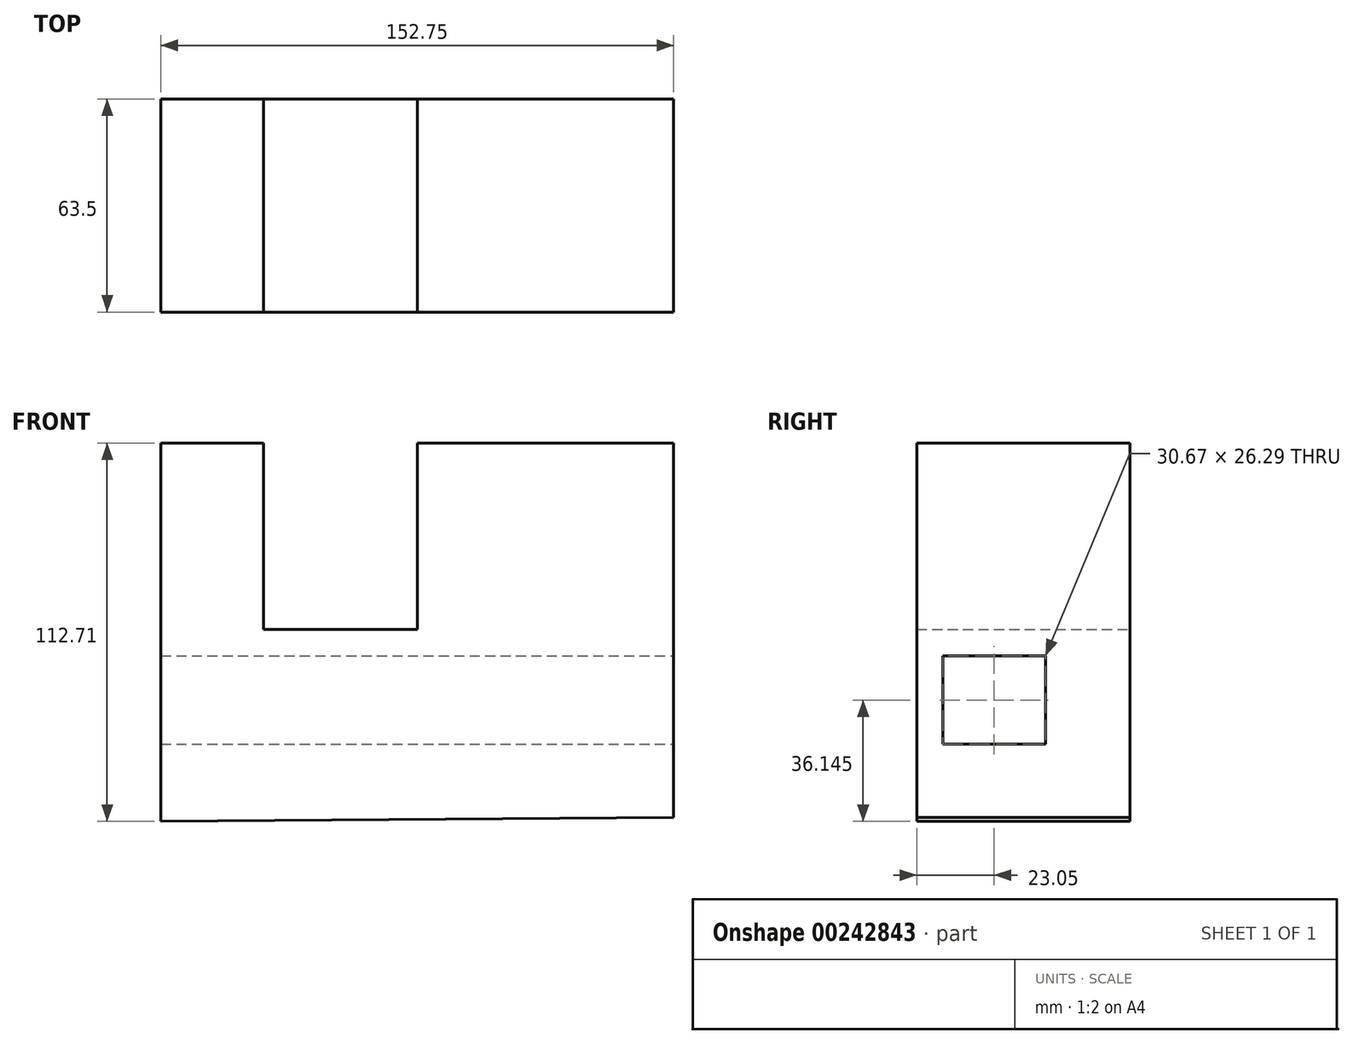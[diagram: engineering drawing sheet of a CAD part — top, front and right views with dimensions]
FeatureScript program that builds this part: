
annotation { "Feature Type Name" : "Feature", "Feature Type Description" : "" }
export const myFeature = defineFeature(function(context is Context, id is Id, definition is map)
    precondition{}
    {
        {
            var Q0;
            Q0=qCreatedBy(makeId("Front.planeOp"),FACE);
            var sketch = newSketch(context, id + "F0", { "sketchPlane" : qUnion([Q0])});
            skLineSegment(sketch, "E0", {"start": v(-76.39, 55.52) * mm, "end": v(-76.39, -57.19) * mm});
            skLineSegment(sketch, "E1", {"start": v(-76.39, 55.52) * mm, "end": v(-45.83, 55.52) * mm});
            skLineSegment(sketch, "E2", {"start": v(-45.83, 55.68) * mm, "end": v(-45.83, 0) * mm});
            skLineSegment(sketch, "E3", {"start": v(-45.83, 0) * mm, "end": v(0, 0) * mm});
            skLineSegment(sketch, "E4", {"start": v(0, 0) * mm, "end": v(0, 55.52) * mm});
            skLineSegment(sketch, "E5", {"start": v(0, 55.52) * mm, "end": v(76.36, 55.52) * mm});
            skLineSegment(sketch, "E6", {"start": v(76.36, 55.52) * mm, "end": v(76.36, -56.02) * mm});
            skLineSegment(sketch, "E7", {"start": v(76.36, -56.02) * mm, "end": v(-76.39, -57.19) * mm});
            skSolve(sketch);
        }
        {
            var Q0;
            Q0=makeQuery(id+"F0.imprint","IMPRINT",FACE,{"disambiguationData":[TD([[makeQuery(id+"F0.imprint","IMPRINT",EDGE,{"derivedFrom":sQuery(id+"F0.wireOp",EDGE,"E0")}),1.0]])]});
            extrude(context, id + "F1", {"entities" : qUnion([Q0]), "depth" : 63.5 * mm});
        }
        {
            var Q0;
            Q0=makeQuery(id+"F1.opExtrude","SWEPT_FACE",FACE,{"disambiguationData":[OSD([sQuery(id+"F0.wireOp",EDGE,"E6")])]});
            var sketch = newSketch(context, id + "F2", { "sketchPlane" : qUnion([Q0])});
            skLineSegment(sketch, "E8.bottom", {"start": v(-55.78, -7.9) * mm, "end": v(-25.12, -7.9) * mm});
            skLineSegment(sketch, "E8.top", {"start": v(-55.78, -34.19) * mm, "end": v(-25.12, -34.19) * mm});
            skLineSegment(sketch, "E8.left", {"start": v(-55.78, -7.9) * mm, "end": v(-55.78, -34.19) * mm});
            skLineSegment(sketch, "E8.right", {"start": v(-25.12, -7.9) * mm, "end": v(-25.12, -34.19) * mm});
            skSolve(sketch);
        }
        {
            var Q0;
            Q0=makeQuery(id+"F2.imprint","IMPRINT",FACE,{"disambiguationData":[TD([[makeQuery(id+"F2.imprint","IMPRINT",EDGE,{"derivedFrom":sQuery(id+"F2.wireOp",EDGE,"E8.bottom")}),-1.0]])]});
            extrude(context, id + "F3", {"entities" : qUnion([Q0]), "operationType" : NewBodyOperationType.REMOVE, "endBound" : BoundingType.THROUGH_ALL, "oppositeDirection" : true, "depth" : 25.4 * mm});
        }
    });
